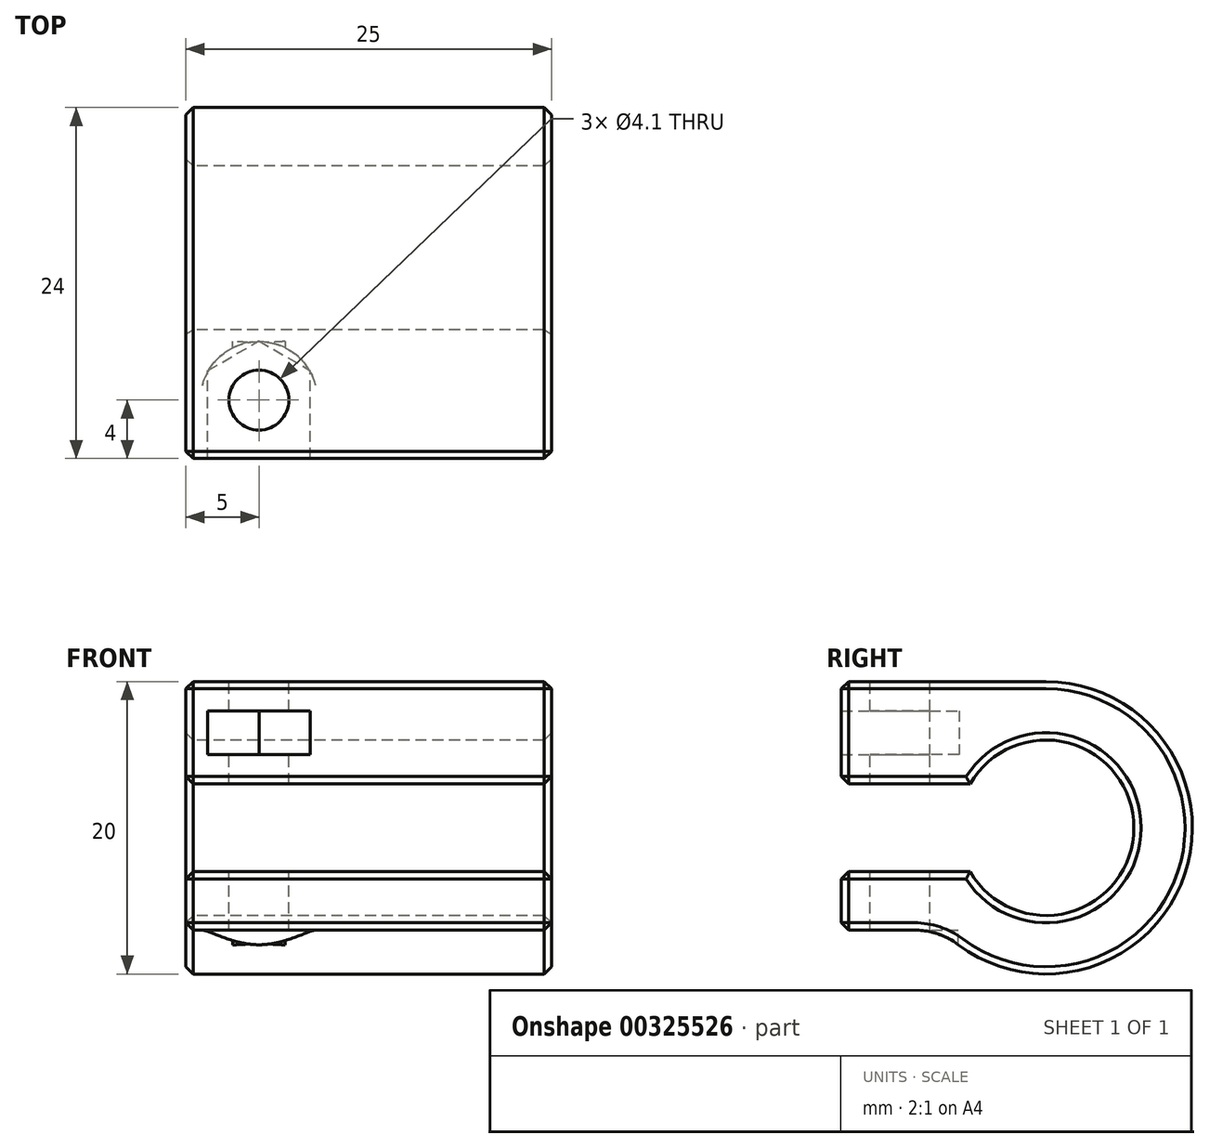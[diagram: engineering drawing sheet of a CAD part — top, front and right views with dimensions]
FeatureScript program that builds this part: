
annotation { "Feature Type Name" : "Feature", "Feature Type Description" : "" }
export const myFeature = defineFeature(function(context is Context, id is Id, definition is map)
    precondition{}
    {
        {
            var Q0;
            Q0=qCreatedBy(makeId("Right.planeOp"),FACE);
            var sketch = newSketch(context, id + "F0", { "sketchPlane" : qUnion([Q0])});
            skArc(sketch, "E0", {"start": v(-5.2, -3) * mm, "mid": v(6, 0) * mm, "end": v(-5.2, 3) * mm});
            skLineSegment(sketch, "E1", {"start": v(-14, 3) * mm, "end": v(-5.2, 3) * mm});
            skLineSegment(sketch, "E2", {"start": v(0, 0) * mm, "end": v(-19.77, 0) * mm, "construction": true});
            skLineSegment(sketch, "E3.MirrorCS", {"start": v(-14, -3) * mm, "end": v(-5.2, -3) * mm});
            skLineSegment(sketch, "E4", {"start": v(0, 10) * mm, "end": v(-14, 10) * mm});
            skLineSegment(sketch, "E5.MirrorCS", {"start": v(-7.14, -7) * mm, "end": v(-14, -7) * mm});
            skLineSegment(sketch, "E6", {"start": v(-14, 10) * mm, "end": v(-14, 3) * mm});
            skLineSegment(sketch, "E7.trimOffspring", {"start": v(-14, -3) * mm, "end": v(-14, -7) * mm});
            skPoint(sketch, "E8.orphan", {"position": v(17.76, 10) * mm});
            skArc(sketch, "E9.trimOffspring", {"start": v(-7.14, -7) * mm, "mid": v(9.22, -3.87) * mm, "end": v(0, 10) * mm});
            skSolve(sketch);
        }
        {
            var Q0;
            Q0 = qSketchRegion(id + "F0", true);
            extrude(context, id + "F1", {"entities" : qUnion([Q0]), "depth" : 25 * mm});
        }
        {
            var Q0;
            Q0=makeQuery(id+"F1.opExtrude","SWEPT_FACE",FACE,{"disambiguationData":[OSD([sQuery(id+"F0.wireOp",EDGE,"E4")])]});
            var sketch = newSketch(context, id + "F2", { "sketchPlane" : qUnion([Q0])});
            skCircle(sketch, "E10", {"center": v(5, -10) * mm, "radius": 2.05 * mm});
            skSolve(sketch);
        }
        {
            var Q0;
            Q0=makeQuery(id+"F2.imprint","IMPRINT",FACE,{"disambiguationData":[TD([[makeQuery(id+"F2.imprint","IMPRINT",EDGE,{"derivedFrom":sQuery(id+"F2.wireOp",EDGE,"E10")}),1.0]])]});
            extrude(context, id + "F3", {"entities" : qUnion([Q0]), "operationType" : NewBodyOperationType.REMOVE, "endBound" : BoundingType.THROUGH_ALL, "oppositeDirection" : true, "depth" : 25 * mm});
        }
        {
            var Q0;
            Q0=makeQuery(id+"F1.opExtrude","SWEPT_EDGE",EDGE,{"disambiguationData":[OSD([sQuery(id+"F0.wireOp",EDGE,"E5.MirrorCS"),sQuery(id+"F0.wireOp",EDGE,"E9.trimOffspring")])]});
            var Q1;
            Q1=makeQuery(id+"F1.opExtrude","SWEPT_EDGE",EDGE,{"disambiguationData":[OSD([sQuery(id+"F0.wireOp",EDGE,"E4"),sQuery(id+"F0.wireOp",EDGE,"E9.trimOffspring")])]});
            fillet(context, id + "F4", {"entities" : qUnion([Q0, Q1]), "radius" : 5 * mm, "tangentPropagation" : true, "allowEdgeOverflow" : false});
        }
        {
            var Q0;
            Q0=makeQuery(id+"F1.opExtrude","CAP_FACE",FACE,{"disambiguationData":[OSD([sQuery(id+"F0.wireOp",EDGE,"E0"),sQuery(id+"F0.wireOp",EDGE,"E1"),sQuery(id+"F0.wireOp",EDGE,"E3.MirrorCS"),sQuery(id+"F0.wireOp",EDGE,"E4"),sQuery(id+"F0.wireOp",EDGE,"E5.MirrorCS"),sQuery(id+"F0.wireOp",EDGE,"E6"),sQuery(id+"F0.wireOp",EDGE,"E7.trimOffspring"),sQuery(id+"F0.wireOp",EDGE,"E9.trimOffspring")])],"isStart":false});
            var Q1;
            Q1=makeQuery(id+"F1.opExtrude","SWEPT_FACE",FACE,{"disambiguationData":[OSD([sQuery(id+"F0.wireOp",EDGE,"E7.trimOffspring")])]});
            var Q2;
            Q2=makeQuery(id+"F1.opExtrude","SWEPT_FACE",FACE,{"disambiguationData":[OSD([sQuery(id+"F0.wireOp",EDGE,"E6")])]});
            var Q3;
            Q3=makeQuery(id+"F1.opExtrude","CAP_FACE",FACE,{"disambiguationData":[OSD([sQuery(id+"F0.wireOp",EDGE,"E0"),sQuery(id+"F0.wireOp",EDGE,"E1"),sQuery(id+"F0.wireOp",EDGE,"E3.MirrorCS"),sQuery(id+"F0.wireOp",EDGE,"E4"),sQuery(id+"F0.wireOp",EDGE,"E5.MirrorCS"),sQuery(id+"F0.wireOp",EDGE,"E6"),sQuery(id+"F0.wireOp",EDGE,"E7.trimOffspring"),sQuery(id+"F0.wireOp",EDGE,"E9.trimOffspring")])],"isStart":true});
            chamfer(context, id + "F5", {"entities" : qUnion([Q0, Q1, Q2, Q3]), "width" : 0.5 * mm, "tangentPropagation" : true});
        }
        {
            var Q0;
            Q0=qCreatedBy(makeId("Top.planeOp"),FACE);
            cPlane(context, id + "F6", {"entities" : qUnion([Q0]), "cplaneType" : CPlaneType.OFFSET, "offset" : 5 * mm, "width" : 150 * mm, "height" : 150 * mm});
        }
        {
            var Q0;
            Q0=qCreatedBy(id+"F6.planeOp",FACE);
            var sketch = newSketch(context, id + "F7", { "sketchPlane" : qUnion([Q0])});
            skLineSegment(sketch, "E11.2", {"start": v(0.5, -5.91) * mm, "end": v(0.5, 10) * mm});
            skPoint(sketch, "E12.0", {"position": v(5, -10) * mm});
            skCircle(sketch, "E13.cCircle", {"center": v(5, -10) * mm, "radius": 3.5 * mm, "construction": true});
            skLineSegment(sketch, "E13.2", {"start": v(1.5, -12.02) * mm, "end": v(1.5, -7.98) * mm});
            skLineSegment(sketch, "E13.3", {"start": v(1.5, -7.98) * mm, "end": v(5, -5.96) * mm});
            skLineSegment(sketch, "E13.4", {"start": v(5, -5.96) * mm, "end": v(8.5, -7.98) * mm});
            skLineSegment(sketch, "E13.5", {"start": v(8.5, -7.98) * mm, "end": v(8.5, -12.04) * mm});
            skPoint(sketch, "E13.0.midPoint", {"position": v(6.75, -13.03) * mm});
            skCircle(sketch, "E14", {"center": v(5, -10) * mm, "radius": 2 * mm});
            skLineSegment(sketch, "E15", {"start": v(1.5, -12.02) * mm, "end": v(1.5, -15) * mm});
            skLineSegment(sketch, "E16", {"start": v(1.5, -15) * mm, "end": v(8.5, -15) * mm});
            skLineSegment(sketch, "E17", {"start": v(8.5, -15) * mm, "end": v(8.5, -12.04) * mm});
            skSolve(sketch);
        }
        {
            var Q0;
            Q0 = qSketchRegion(id + "F7", true);
            extrude(context, id + "F8", {"entities" : qUnion([Q0]), "depth" : 3 * mm});
        }
        {
            var Q0;
            Q0=makeQuery(id+"F2.imprint","IMPRINT",FACE,{"disambiguationData":[TD([[makeQuery(id+"F2.imprint","IMPRINT",EDGE,{"derivedFrom":sQuery(id+"F2.wireOp",EDGE,"E10")}),-1.0]])]});
            var sketch = newSketch(context, id + "F9", { "sketchPlane" : qUnion([Q0])});
            skCircle(sketch, "E18.0", {"center": v(5, -10) * mm, "radius": 2.05 * mm});
            skCircle(sketch, "E19", {"center": v(5, -10) * mm, "radius": 4 * mm});
            skSolve(sketch);
        }
        {
            var Q0;
            Q0 = qSketchRegion(id + "F9", true);
            extrude(context, id + "F10", {"entities" : qUnion([Q0]), "operationType" : NewBodyOperationType.REMOVE, "depth" : 25 * mm});
        }
        {
            var Q0;
            Q0=makeQuery(id+"F1.opExtrude","SWEPT_FACE",FACE,{"disambiguationData":[OSD([sQuery(id+"F0.wireOp",EDGE,"E5.MirrorCS")])]});
            var sketch = newSketch(context, id + "F11", { "sketchPlane" : qUnion([Q0])});
            skCircle(sketch, "E20.0", {"center": v(5, 10) * mm, "radius": 2.05 * mm});
            skCircle(sketch, "E21", {"center": v(5, 10) * mm, "radius": 4 * mm});
            skSolve(sketch);
        }
        {
            var Q0;
            Q0 = qSketchRegion(id + "F11", true);
            extrude(context, id + "F12", {"entities" : qUnion([Q0]), "operationType" : NewBodyOperationType.REMOVE, "depth" : 25 * mm});
        }
        {
            var Q0;
            Q0=makeQuery(id+"F8.opExtrude","SWEPT_BODY",BODY,{"disambiguationData":[OSD([sQuery(id+"F7.wireOp",EDGE,"E13.2"),sQuery(id+"F7.wireOp",EDGE,"E13.3"),sQuery(id+"F7.wireOp",EDGE,"E13.4"),sQuery(id+"F7.wireOp",EDGE,"E13.5"),sQuery(id+"F7.wireOp",EDGE,"E14"),sQuery(id+"F7.wireOp",EDGE,"E15"),sQuery(id+"F7.wireOp",EDGE,"E16"),sQuery(id+"F7.wireOp",EDGE,"E17")])]});
            var Q1;
            Q1=makeQuery(id+"F1.opExtrude","SWEPT_BODY",BODY,{"disambiguationData":[OSD([sQuery(id+"F0.wireOp",EDGE,"E0"),sQuery(id+"F0.wireOp",EDGE,"E1"),sQuery(id+"F0.wireOp",EDGE,"E3.MirrorCS"),sQuery(id+"F0.wireOp",EDGE,"E4"),sQuery(id+"F0.wireOp",EDGE,"E5.MirrorCS"),sQuery(id+"F0.wireOp",EDGE,"E6"),sQuery(id+"F0.wireOp",EDGE,"E7.trimOffspring"),sQuery(id+"F0.wireOp",EDGE,"E9.trimOffspring")])]});
            booleanBodies(context, id + "F13", {"operationType" : BooleanOperationType.SUBTRACTION, "tools" : qUnion([Q0]), "targets" : qUnion([Q1])});
        }
    });
